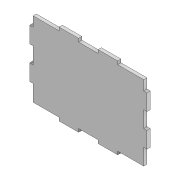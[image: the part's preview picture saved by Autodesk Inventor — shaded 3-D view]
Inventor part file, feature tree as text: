
AUTODESK INVENTOR PART (.ipt)
format: ipt  version: 2022 (Build 260153000, 153)  size: 121,344 bytes
history: native  units: mm
features: extrude x1, sketch x1
ambient origin geometry x8: Origin, YZ Plane, XZ Plane, XY Plane, X Axis, Y Axis, Z Axis, Center Point
bodies: Solid1 (feature_tree)
feature tree (2):
  extrude  "Extrusion1"  Depth=115.0mm
  sketch  "Sketch1"  dims[d0=170.0mm d1=115.0mm d2=30.0mm d3=5.0mm d4=30.0mm d5=5.0mm d6=30.0mm d7=40.0mm d8=5.0mm d9=25.0mm d10=5.0mm d11=25.0mm d12=25.0mm d13=15.0mm d14=5.0mm d15=0.0mm]
